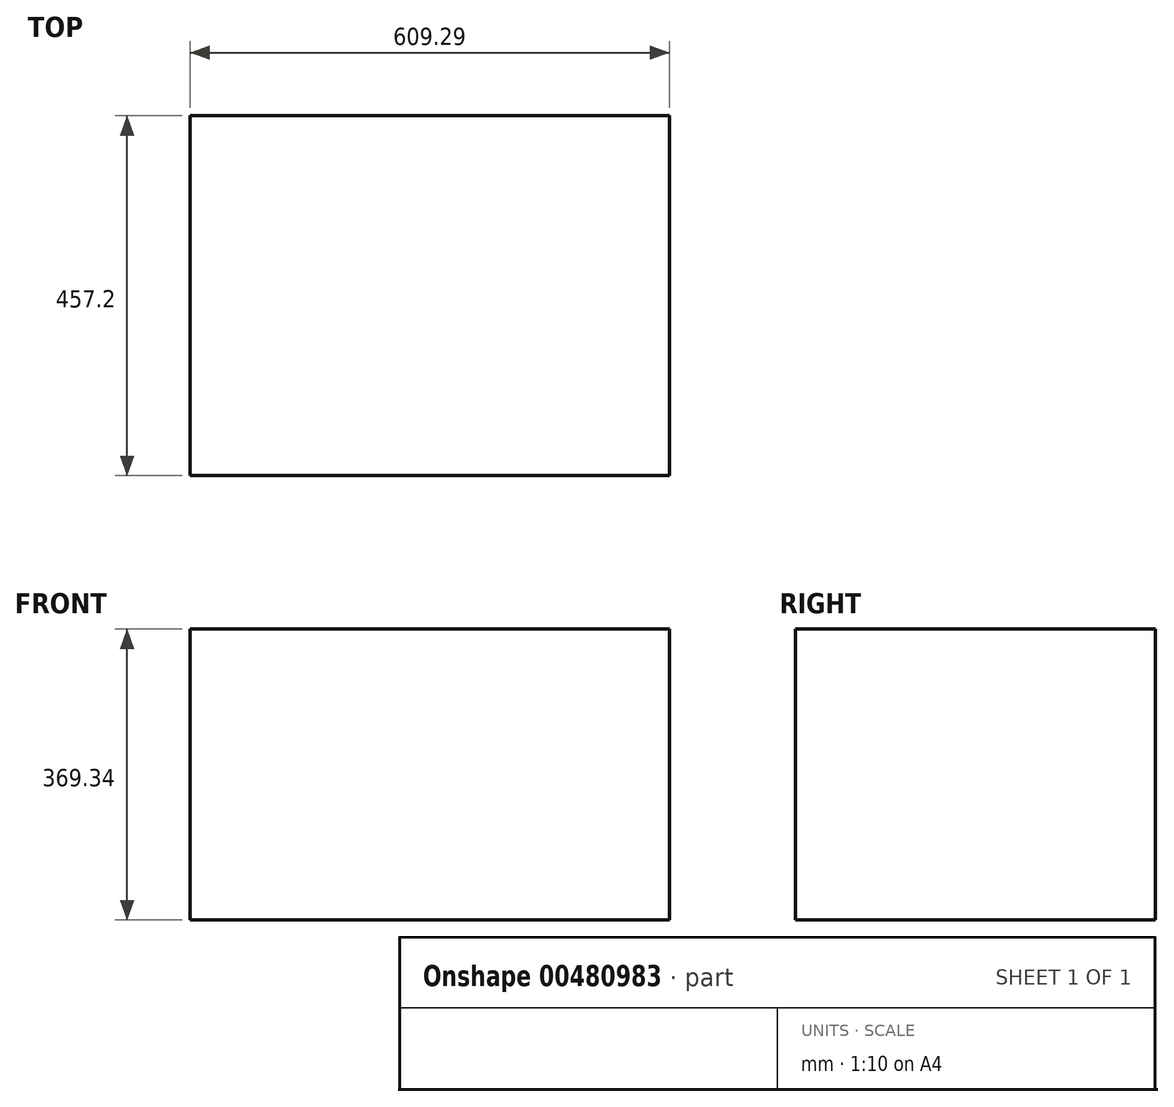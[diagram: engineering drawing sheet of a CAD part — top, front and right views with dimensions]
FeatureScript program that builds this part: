
annotation { "Feature Type Name" : "Feature", "Feature Type Description" : "" }
export const myFeature = defineFeature(function(context is Context, id is Id, definition is map)
    precondition{}
    {
        {
            var Q0;
            Q0=qCreatedBy(makeId("Front.planeOp"),FACE);
            var sketch = newSketch(context, id + "F0", { "sketchPlane" : qUnion([Q0])});
            skLineSegment(sketch, "E0.bottom", {"start": v(-366.51, 125.31) * mm, "end": v(242.78, 125.31) * mm});
            skLineSegment(sketch, "E0.top", {"start": v(-366.51, -244.03) * mm, "end": v(242.78, -244.03) * mm});
            skLineSegment(sketch, "E0.left", {"start": v(-366.51, 125.31) * mm, "end": v(-366.51, -244.03) * mm});
            skLineSegment(sketch, "E0.right", {"start": v(242.78, 125.31) * mm, "end": v(242.78, -244.03) * mm});
            skSolve(sketch);
        }
        {
            var Q0;
            Q0=makeQuery(id+"F0.imprint","IMPRINT",FACE,{"disambiguationData":[TD([[makeQuery(id+"F0.imprint","IMPRINT",EDGE,{"derivedFrom":sQuery(id+"F0.wireOp",EDGE,"E0.bottom")}),-1.0]])]});
            extrude(context, id + "F1", {"entities" : qUnion([Q0]), "depth" : 457.2 * mm});
        }
    });
